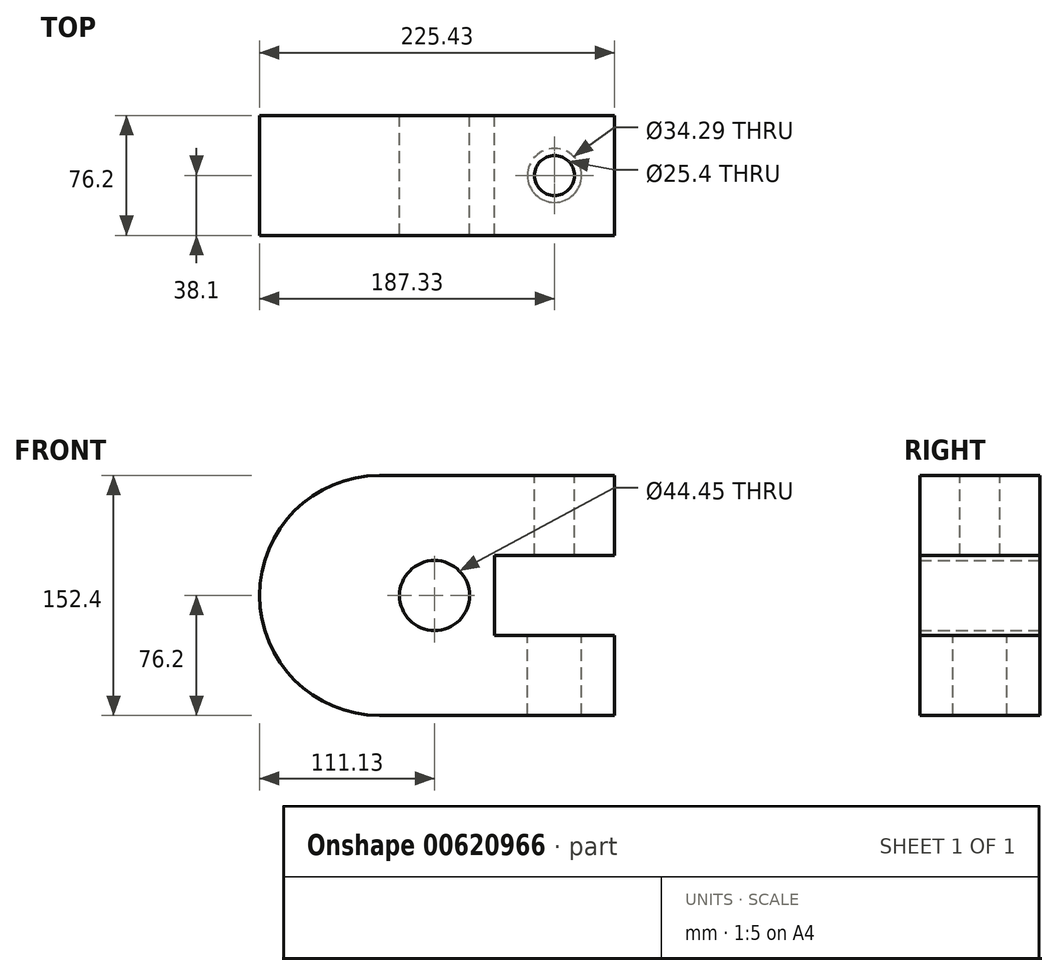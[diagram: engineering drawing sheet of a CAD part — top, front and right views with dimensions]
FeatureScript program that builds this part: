
annotation { "Feature Type Name" : "Feature", "Feature Type Description" : "" }
export const myFeature = defineFeature(function(context is Context, id is Id, definition is map)
    precondition{}
    {
        {
            var Q0;
            Q0=qCreatedBy(makeId("Front.planeOp"),FACE);
            var sketch = newSketch(context, id + "F0", { "sketchPlane" : qUnion([Q0])});
            skLineSegment(sketch, "E0", {"start": v(0, 0) * mm, "end": v(-149.23, 0) * mm});
            skLineSegment(sketch, "E1", {"start": v(-149.23, 152.4) * mm, "end": v(0, 152.4) * mm});
            skLineSegment(sketch, "E2", {"start": v(0, 152.4) * mm, "end": v(0, 101.6) * mm});
            skLineSegment(sketch, "E3", {"start": v(0, 101.6) * mm, "end": v(-76.2, 101.6) * mm});
            skLineSegment(sketch, "E4", {"start": v(-76.2, 101.6) * mm, "end": v(-76.2, 50.8) * mm});
            skLineSegment(sketch, "E5", {"start": v(-76.2, 50.8) * mm, "end": v(0, 50.8) * mm});
            skLineSegment(sketch, "E6", {"start": v(0, 50.8) * mm, "end": v(0, 0) * mm});
            skArc(sketch, "E7", {"start": v(-149.23, 152.4) * mm, "mid": v(-225.43, 76.2) * mm, "end": v(-149.23, 0) * mm});
            skCircle(sketch, "E8", {"center": v(-114.3, 76.2) * mm, "radius": 22.23 * mm});
            skSolve(sketch);
        }
        {
            var Q0;
            Q0=makeQuery(id+"F0.imprint","IMPRINT",FACE,{"disambiguationData":[TD([[makeQuery(id+"F0.imprint","IMPRINT",EDGE,{"derivedFrom":sQuery(id+"F0.wireOp",EDGE,"E0")}),-1.0]])]});
            extrude(context, id + "F1", {"entities" : qUnion([Q0]), "depth" : 76.2 * mm, "offsetDistance" : 25.4 * mm});
        }
        {
            var Q0;
            Q0=makeQuery(id+"F1.opExtrude","SWEPT_FACE",FACE,{"disambiguationData":[OSD([sQuery(id+"F0.wireOp",EDGE,"E5")])]});
            var sketch = newSketch(context, id + "F2", { "sketchPlane" : qUnion([Q0])});
            skSolve(sketch);
        }
        {
            var Q0;
            {var subQ0=sQuery(id+"F0.wireOp",EDGE,"E5");Q0=makeQuery(id+"F2.imprint","IMPRINT",FACE,{"disambiguationData":[TD([[makeQuery(id+"F2.imprint","IMPRINT",EDGE,{"derivedFrom":makeQuery(id+"F1.opExtrude","CAP_EDGE",EDGE,{"disambiguationData":[OSD([subQ0])],"isStart":true})}),-1.0]])]});}
            var sketch = newSketch(context, id + "F3", { "sketchPlane" : qUnion([Q0])});
            skCircle(sketch, "E9", {"center": v(-38.1, -38.1) * mm, "radius": 8.57 * mm});
            skSolve(sketch);
        }
        {
            var Q0;
            Q0=sQuery(id+"F3.wireOp",VERTEX,"E9.center");
            var Q1;
            Q1=makeQuery(id+"F1.opExtrude","SWEPT_BODY",BODY,{"disambiguationData":[OSD([sQuery(id+"F0.wireOp",EDGE,"E0"),sQuery(id+"F0.wireOp",EDGE,"E1"),sQuery(id+"F0.wireOp",EDGE,"E2"),sQuery(id+"F0.wireOp",EDGE,"E3"),sQuery(id+"F0.wireOp",EDGE,"E4"),sQuery(id+"F0.wireOp",EDGE,"E5"),sQuery(id+"F0.wireOp",EDGE,"E6"),sQuery(id+"F0.wireOp",EDGE,"E7"),sQuery(id+"F0.wireOp",EDGE,"E8")])]});
            hole(context, id + "F4", {"style" : HoleStyle.SIMPLE, "endStyle" : HoleEndStyle.THROUGH, "holeDiameter" : 34.3 * mm, "majorDiameter" : 6.35 * mm, "isTappedThrough" : true, "tappedDepth" : 12.7 * mm, "tapClearance" : 3, "locations" : qUnion([Q0]), "scope" : qUnion([Q1])});
        }
        {
            var Q0;
            Q0=makeQuery(id+"F1.opExtrude","SWEPT_FACE",FACE,{"disambiguationData":[OSD([sQuery(id+"F0.wireOp",EDGE,"E1")])]});
            var sketch = newSketch(context, id + "F5", { "sketchPlane" : qUnion([Q0])});
            skCircle(sketch, "E10", {"center": v(-38.1, -38.1) * mm, "radius": 6.35 * mm});
            skSolve(sketch);
        }
        {
            var Q0;
            Q0=sQuery(id+"F5.wireOp",VERTEX,"E10.center");
            var Q1;
            Q1=makeQuery(id+"F1.opExtrude","SWEPT_BODY",BODY,{"disambiguationData":[OSD([sQuery(id+"F0.wireOp",EDGE,"E0"),sQuery(id+"F0.wireOp",EDGE,"E1"),sQuery(id+"F0.wireOp",EDGE,"E2"),sQuery(id+"F0.wireOp",EDGE,"E3"),sQuery(id+"F0.wireOp",EDGE,"E4"),sQuery(id+"F0.wireOp",EDGE,"E5"),sQuery(id+"F0.wireOp",EDGE,"E6"),sQuery(id+"F0.wireOp",EDGE,"E7"),sQuery(id+"F0.wireOp",EDGE,"E8")])]});
            hole(context, id + "F6", {"style" : HoleStyle.SIMPLE, "endStyle" : HoleEndStyle.THROUGH, "holeDiameter" : 25.4 * mm, "majorDiameter" : 6.35 * mm, "isTappedThrough" : true, "tappedDepth" : 12.7 * mm, "tapClearance" : 3, "locations" : qUnion([Q0]), "scope" : qUnion([Q1])});
        }
    });
